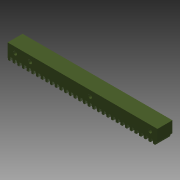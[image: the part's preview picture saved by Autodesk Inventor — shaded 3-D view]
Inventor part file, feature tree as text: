
AUTODESK INVENTOR PART (.ipt)
format: ipt  version: 2015 SP1 (Build 190203100, 203)  size: 226,816 bytes
history: native  units: in
note: dims shown in document units (in); Inventor stores cm internally (conversion verified against a paired STEP export)
features: sketch x3, extrude x2, pattern_linear x1, hole x1, projected_geometry x1
ambient origin geometry x8: Origin, YZ Plane, XZ Plane, XY Plane, X Axis, Y Axis, Z Axis, Center Point
bodies: Solid1 (feature_tree)
feature tree (8):
  extrude  "Extrusion1"  Depth=1.0in
  extrude  "Extrusion3"  Depth=10.0in
  pattern_linear  "Rectangular Pattern2"  Spacing1=0.125in  [1 undecoded]
  hole  "Hole3"  [1 undecoded]
  sketch  "Sketch1"  dims[d0=1.0in d1=1.0in]
  sketch  "Sketch2"  dims[d2=10.0in d3=0.0in d4=0.0312in]
  projected_geometry  "Projected Loop1"
  sketch  "Sketch4"  dims[d5=0.25in d6=0.125in d7=0.25in d8=0.0312in d9=0.25in d10=0.125in d11=0.25in d17=1.0in d18=0.0in d19=12.5984in d21=0.3125in d33=0.5in d34=0.375in d35=0.375in d44=0.5in d45=1.5in d46=4.5in d47=0.375in d48=0.375in d49=0.25in d50=0.75in d51=0.375in d52=0.25in d53=0.5635in d54=1.0in d55=0.8108in]
note: 2 required parameter values undecoded (feature->parameter linkage not recoverable at this tier; creation-order binding heuristic only, values carry confidence <= 0.55)
